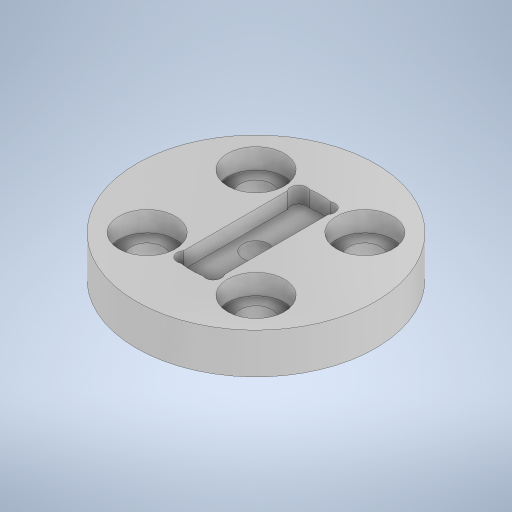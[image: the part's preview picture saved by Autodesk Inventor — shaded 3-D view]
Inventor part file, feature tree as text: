
AUTODESK INVENTOR PART (.ipt)
format: ipt  version: 2024.2 (Build 282272000, 272)  size: 318,976 bytes
history: native  units: mm
features: hole x3, extrude x2, sketch x1
ambient origin geometry x8: Origin, YZ Plane, XZ Plane, XY Plane, X Axis, Y Axis, Z Axis, Center Point
bodies: Solid1 (feature_tree)
feature tree (6):
  sketch  "Sketch1"  dims[d1=16.0mm d2=5.0mm d3=25.0mm d4=29.5mm d7=45.0deg d9=40.0mm d11=360.0deg d13=5.0mm d14=0.0mm d15=3.2mm d16=6.0mm d17=4.0mm d18=3.5mm d19=90.0deg d20=8.0mm d21=20.594885mm d22=3.5mm d23=6.0mm d24=6.5mm d25=3.5mm d26=90.0deg d27=8.0mm d28=20.594885mm d29=4.0mm d30=6.0mm d31=7.0mm d32=2.5mm d33=90.0deg d34=8.0mm d35=20.594885mm d36=5.5mm d37=0.5mm d39=4.0mm d40=0.0mm d41=0.025mm d42=0.025mm d43=1.0mm d44=2.0mm d45=0.0mm d47=3.5mm d48=0.5mm d49=1.0mm d50=40.0mm d52=360.0deg d56=1.0mm d57=6.5mm d46=0.75mm d58=1.0mm d59=1.0mm d60=0.15mm d61=0.25mm d62=0.375mm d63=14.3117mm d64=0.75mm d65=20.594885mm d66=0.0625mm d67=0.75mm d68=0.375mm]
  extrude  "Extrusion1"  Depth=5.0mm
  hole  "Hole1"  [1 undecoded]
  hole  "Hole2"  [1 undecoded]
  hole  "Hole3"  [1 undecoded]
  extrude  "Extrusion2"  Depth=1.0mm TaperAngle=360.0deg
note: 3 required parameter values undecoded (feature->parameter linkage not recoverable at this tier; creation-order binding heuristic only, values carry confidence <= 0.55)
